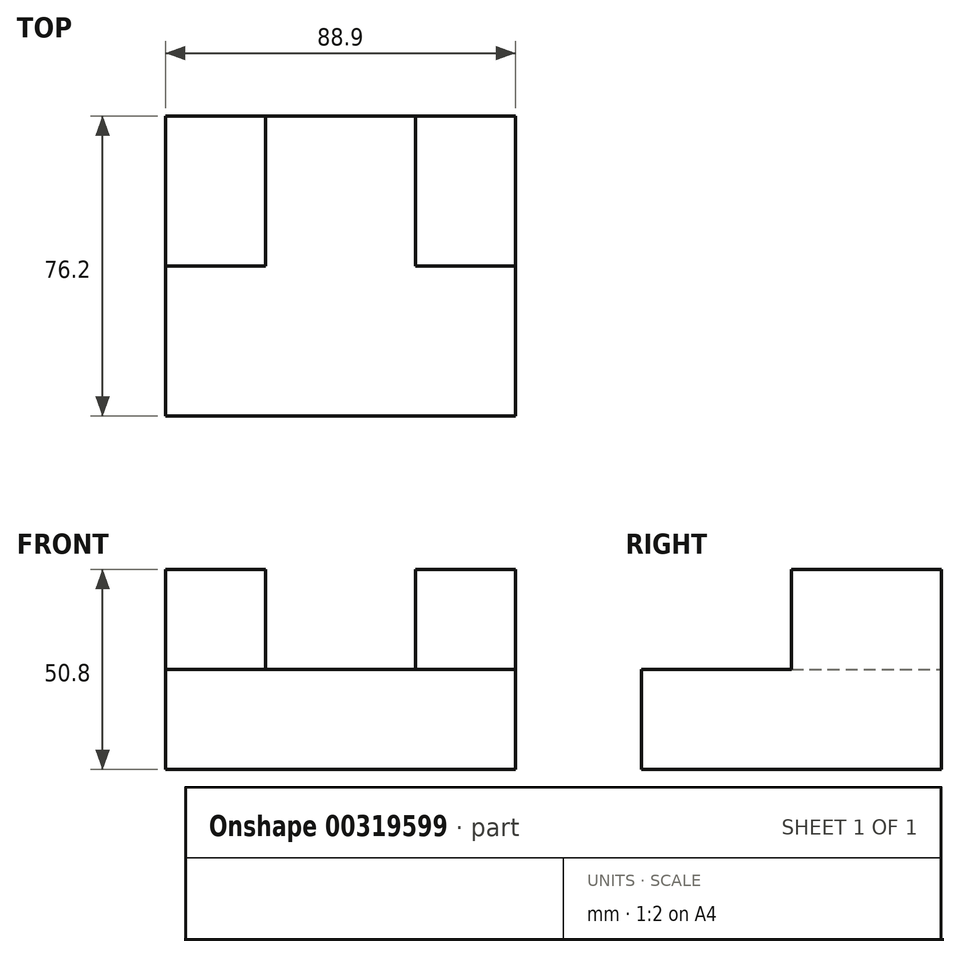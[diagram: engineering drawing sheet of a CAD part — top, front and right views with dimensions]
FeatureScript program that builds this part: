
annotation { "Feature Type Name" : "Feature", "Feature Type Description" : "" }
export const myFeature = defineFeature(function(context is Context, id is Id, definition is map)
    precondition{}
    {
        {
            var Q0;
            Q0=qCreatedBy(makeId("Front.planeOp"),FACE);
            var sketch = newSketch(context, id + "F0", { "sketchPlane" : qUnion([Q0])});
            skLineSegment(sketch, "E0", {"start": v(-25.1, -50.8) * mm, "end": v(63.8, -50.8) * mm});
            skLineSegment(sketch, "E1", {"start": v(63.8, -50.8) * mm, "end": v(63.8, -25.4) * mm});
            skLineSegment(sketch, "E2", {"start": v(63.8, -25.4) * mm, "end": v(-25.1, -25.4) * mm});
            skLineSegment(sketch, "E3", {"start": v(-25.1, -25.4) * mm, "end": v(-25.1, -50.8) * mm});
            skLineSegment(sketch, "E4", {"start": v(-25.1, -25.4) * mm, "end": v(-25.1, 0) * mm});
            skLineSegment(sketch, "E5", {"start": v(-25.1, 0) * mm, "end": v(0.3, 0) * mm});
            skLineSegment(sketch, "E6", {"start": v(0.3, 0) * mm, "end": v(0.3, -25.4) * mm});
            skLineSegment(sketch, "E7", {"start": v(0.3, -25.4) * mm, "end": v(-25.1, -25.4) * mm});
            skLineSegment(sketch, "E8", {"start": v(63.8, -25.4) * mm, "end": v(63.8, 0) * mm});
            skLineSegment(sketch, "E9", {"start": v(63.8, 0) * mm, "end": v(38.4, 0) * mm});
            skLineSegment(sketch, "E10", {"start": v(38.4, 0) * mm, "end": v(38.4, -25.4) * mm});
            skLineSegment(sketch, "E11", {"start": v(38.4, -25.4) * mm, "end": v(63.8, -25.4) * mm});
            skSolve(sketch);
        }
        {
            var Q0;
            Q0=makeQuery(id+"F0.imprint","IMPRINT",FACE,{"disambiguationData":[TD([[makeQuery(id+"F0.imprint","IMPRINT",EDGE,{"derivedFrom":sQuery(id+"F0.wireOp",EDGE,"E0")}),1.0]])]});
            extrude(context, id + "F1", {"entities" : qUnion([Q0]), "depth" : 76.2 * mm});
        }
        {
            var Q0;
            Q0 = qSketchRegion(id + "F0", true);
            extrude(context, id + "F2", {"entities" : qUnion([Q0]), "operationType" : NewBodyOperationType.ADD, "depth" : 38.1 * mm});
        }
    });
